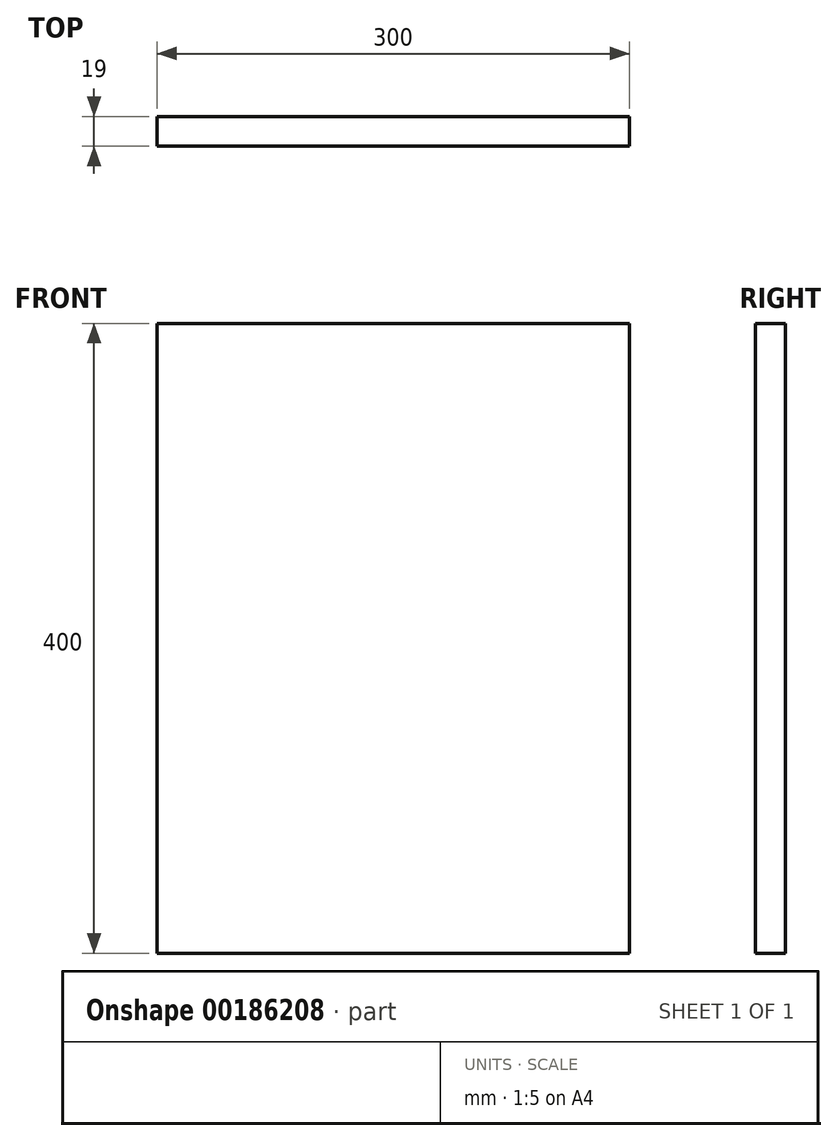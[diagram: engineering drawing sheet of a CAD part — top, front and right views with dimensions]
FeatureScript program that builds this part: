
annotation { "Feature Type Name" : "Feature", "Feature Type Description" : "" }
export const myFeature = defineFeature(function(context is Context, id is Id, definition is map)
    precondition{}
    {
        {
            var Q0;
            Q0=qCreatedBy(makeId("Front.planeOp"),FACE);
            var sketch = newSketch(context, id + "F0", { "sketchPlane" : qUnion([Q0])});
            skLineSegment(sketch, "E0.bottom", {"start": v(-150.24, 246.46) * mm, "end": v(149.76, 246.46) * mm});
            skLineSegment(sketch, "E0.top", {"start": v(-150.24, -153.54) * mm, "end": v(149.76, -153.54) * mm});
            skLineSegment(sketch, "E0.left", {"start": v(-150.24, 246.46) * mm, "end": v(-150.24, -153.54) * mm});
            skLineSegment(sketch, "E0.right", {"start": v(149.76, 246.46) * mm, "end": v(149.76, -153.54) * mm});
            skSolve(sketch);
        }
        {
            var Q0;
            Q0 = qSketchRegion(id + "F0", true);
            extrude(context, id + "F1", {"entities" : qUnion([Q0]), "depth" : 19 * mm});
        }
    });
